# Revit family: Mini Wall Mount 1925 -8 MB
name_source: partatom
category: Lighting Fixtures
units: mm (PartAtom-declared; Revit-internal decimal feet)

## family parameters
Always vertical = Yes
Cut with Voids When Loaded = No
Light Source = Yes
OmniClass Number = 23.80.70.00
OmniClass Title = Lighting
Part Type = Normal
Room Calculation Point = No
Round Connector Dimension = Use Diameter
Shared = No
Work Plane-Based = No

## types (1)
- WM1925
    Apparent Load = 100 VA
    Body Colour = Spun aluminium
    Body Material = body
    Bulb = Bulb
    Color Filter = 16777215
    Construction Material = Heavy Duty spun aluminum.
    Default Elevation = 0' - 0"
    Description = 120-277 Voltage
    Dimming Lamp Color Temperature Shift = <None>
    Fixture Diameter = 0' - 9"
    Fixture Height = 0' - 9 1/2"
    INSIDE BODY = INSIDE BODY
    Lamp = MB
    Load Classification = Lighting
    Manufacturer = ANP Lighting
    Model = WM1925
    Photometric Web File = generic.ies
    Power Factor = 1
    Tilt Angle = 90.00°
    URL = https://www.anplighting.com
    Voltage = 277 V
    WM1925 = Yes
    Warranty = 5 year limited warranty
    Wattage Comments = 100W Max
    Weight = 2.0 lbs

## geometry (parser evidence)
native form markers: Sweep x5
no freeform markers — native parametric forms only
